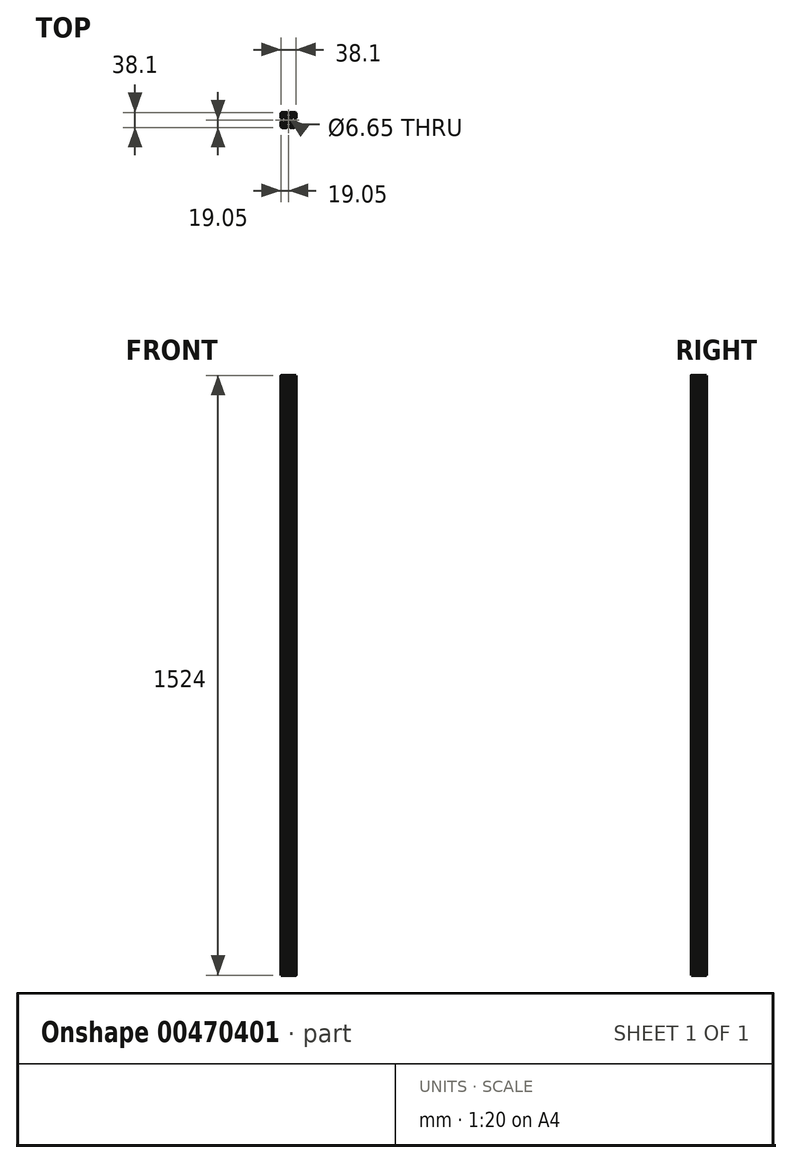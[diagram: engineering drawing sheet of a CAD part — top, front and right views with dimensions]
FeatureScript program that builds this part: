
annotation { "Feature Type Name" : "Feature", "Feature Type Description" : "" }
export const myFeature = defineFeature(function(context is Context, id is Id, definition is map)
    precondition{}
    {
        {
            var Q0;
            Q0=qCreatedBy(makeId("Top.planeOp"),FACE);
            var sketch = newSketch(context, id + "F0", { "sketchPlane" : qUnion([Q0])});
            skCircle(sketch, "E0", {"center": v(0, 0) * mm, "radius": 3.33 * mm});
            skArc(sketch, "E1", {"start": v(-10.29, 13.55) * mm, "mid": v(-10.22, 13.2) * mm, "end": v(-10.02, 12.91) * mm});
            skLineSegment(sketch, "E2", {"start": v(-10.29, 13.55) * mm, "end": v(-10.29, 14.08) * mm});
            skArc(sketch, "E3", {"start": v(-9.39, 14.99) * mm, "mid": v(-10.02, 14.72) * mm, "end": v(-10.29, 14.08) * mm});
            skLineSegment(sketch, "E4", {"start": v(-9.39, 14.99) * mm, "end": v(-5.62, 14.99) * mm});
            skArc(sketch, "E5", {"start": v(-5.62, 14.99) * mm, "mid": v(-4.52, 15.44) * mm, "end": v(-4.06, 16.54) * mm});
            skLineSegment(sketch, "E6", {"start": v(-4.06, 16.54) * mm, "end": v(-4.06, 17.5) * mm});
            skArc(sketch, "E7", {"start": v(-4.06, 17.5) * mm, "mid": v(-4.52, 18.6) * mm, "end": v(-5.62, 19.05) * mm});
            skLineSegment(sketch, "E8", {"start": v(-5.62, 19.05) * mm, "end": v(-7.97, 19.05) * mm});
            skArc(sketch, "E9", {"start": v(-9.5, 19.05) * mm, "mid": v(-8.74, 18.29) * mm, "end": v(-7.97, 19.05) * mm});
            skLineSegment(sketch, "E10", {"start": v(-9.5, 19.05) * mm, "end": v(-14.33, 19.05) * mm});
            skArc(sketch, "E11", {"start": v(-15.85, 19.05) * mm, "mid": v(-15.09, 18.23) * mm, "end": v(-14.33, 19.05) * mm});
            skArc(sketch, "E12", {"start": v(-15.85, 19.05) * mm, "mid": v(-18.12, 18.12) * mm, "end": v(-19.05, 15.85) * mm});
            skArc(sketch, "E13", {"start": v(-19.05, 14.33) * mm, "mid": v(-18.23, 15.09) * mm, "end": v(-19.05, 15.85) * mm});
            skLineSegment(sketch, "E14", {"start": v(-19.05, 14.33) * mm, "end": v(-19.05, 9.5) * mm});
            skArc(sketch, "E15", {"start": v(-19.05, 7.98) * mm, "mid": v(-18.23, 8.74) * mm, "end": v(-19.05, 9.5) * mm});
            skLineSegment(sketch, "E16", {"start": v(-19.05, 7.98) * mm, "end": v(-19.05, 5.62) * mm});
            skArc(sketch, "E17", {"start": v(-19.05, 5.62) * mm, "mid": v(-18.6, 4.52) * mm, "end": v(-17.5, 4.06) * mm});
            skLineSegment(sketch, "E18", {"start": v(-17.5, 4.06) * mm, "end": v(-16.54, 4.06) * mm});
            skArc(sketch, "E19", {"start": v(-16.54, 4.06) * mm, "mid": v(-15.44, 4.52) * mm, "end": v(-14.99, 5.62) * mm});
            skLineSegment(sketch, "E20", {"start": v(-14.99, 5.62) * mm, "end": v(-14.99, 9.39) * mm});
            skArc(sketch, "E21", {"start": v(-14.08, 10.29) * mm, "mid": v(-14.72, 10.02) * mm, "end": v(-14.99, 9.39) * mm});
            skLineSegment(sketch, "E22", {"start": v(-14.08, 10.29) * mm, "end": v(-13.52, 10.29) * mm});
            skArc(sketch, "E23", {"start": v(-12.88, 10.02) * mm, "mid": v(-13.17, 10.22) * mm, "end": v(-13.52, 10.29) * mm});
            skLineSegment(sketch, "E24", {"start": v(-12.88, 10.02) * mm, "end": v(-8.15, 5.3) * mm});
            skArc(sketch, "E25", {"start": v(-6.76, 1.93) * mm, "mid": v(-7.12, 3.75) * mm, "end": v(-8.15, 5.3) * mm});
            skLineSegment(sketch, "E26", {"start": v(-6.76, 1.93) * mm, "end": v(-6.76, -1.93) * mm});
            skArc(sketch, "E27", {"start": v(-8.15, -5.3) * mm, "mid": v(-7.12, -3.75) * mm, "end": v(-6.76, -1.93) * mm});
            skLineSegment(sketch, "E28", {"start": v(-8.15, -5.3) * mm, "end": v(-12.88, -10.02) * mm});
            skArc(sketch, "E29", {"start": v(-13.52, -10.29) * mm, "mid": v(-13.17, -10.22) * mm, "end": v(-12.88, -10.02) * mm});
            skLineSegment(sketch, "E30", {"start": v(-13.52, -10.29) * mm, "end": v(-14.08, -10.29) * mm});
            skArc(sketch, "E31", {"start": v(-14.99, -9.39) * mm, "mid": v(-14.72, -10.02) * mm, "end": v(-14.08, -10.29) * mm});
            skLineSegment(sketch, "E32", {"start": v(-14.99, -9.39) * mm, "end": v(-14.99, -5.62) * mm});
            skArc(sketch, "E33", {"start": v(-14.99, -5.62) * mm, "mid": v(-15.44, -4.52) * mm, "end": v(-16.54, -4.06) * mm});
            skLineSegment(sketch, "E34", {"start": v(-16.54, -4.06) * mm, "end": v(-17.5, -4.06) * mm});
            skArc(sketch, "E35", {"start": v(-17.5, -4.06) * mm, "mid": v(-18.6, -4.52) * mm, "end": v(-19.05, -5.62) * mm});
            skLineSegment(sketch, "E36", {"start": v(-19.05, -5.62) * mm, "end": v(-19.05, -7.98) * mm});
            skArc(sketch, "E37", {"start": v(-19.05, -9.5) * mm, "mid": v(-18.23, -8.74) * mm, "end": v(-19.05, -7.98) * mm});
            skLineSegment(sketch, "E38", {"start": v(-19.05, -9.5) * mm, "end": v(-19.05, -14.33) * mm});
            skArc(sketch, "E39", {"start": v(-19.05, -15.85) * mm, "mid": v(-18.23, -15.09) * mm, "end": v(-19.05, -14.33) * mm});
            skArc(sketch, "E40", {"start": v(-19.05, -15.85) * mm, "mid": v(-18.12, -18.12) * mm, "end": v(-15.85, -19.05) * mm});
            skArc(sketch, "E41", {"start": v(-14.33, -19.05) * mm, "mid": v(-15.09, -18.23) * mm, "end": v(-15.85, -19.05) * mm});
            skLineSegment(sketch, "E42", {"start": v(-14.33, -19.05) * mm, "end": v(-9.5, -19.05) * mm});
            skArc(sketch, "E43", {"start": v(-7.98, -19.05) * mm, "mid": v(-8.74, -18.23) * mm, "end": v(-9.5, -19.05) * mm});
            skLineSegment(sketch, "E44", {"start": v(-7.98, -19.05) * mm, "end": v(-5.62, -19.05) * mm});
            skArc(sketch, "E45", {"start": v(-5.62, -19.05) * mm, "mid": v(-4.52, -18.6) * mm, "end": v(-4.06, -17.5) * mm});
            skLineSegment(sketch, "E46", {"start": v(-4.06, -17.5) * mm, "end": v(-4.06, -16.54) * mm});
            skArc(sketch, "E47", {"start": v(-4.06, -16.54) * mm, "mid": v(-4.52, -15.44) * mm, "end": v(-5.62, -14.99) * mm});
            skLineSegment(sketch, "E48", {"start": v(-5.62, -14.99) * mm, "end": v(-9.39, -14.99) * mm});
            skArc(sketch, "E49", {"start": v(-10.29, -14.08) * mm, "mid": v(-10.02, -14.72) * mm, "end": v(-9.39, -14.99) * mm});
            skLineSegment(sketch, "E50", {"start": v(-10.29, -14.08) * mm, "end": v(-10.29, -13.55) * mm});
            skArc(sketch, "E51", {"start": v(-10.02, -12.91) * mm, "mid": v(-10.22, -13.2) * mm, "end": v(-10.29, -13.55) * mm});
            skLineSegment(sketch, "E52", {"start": v(-10.02, -12.91) * mm, "end": v(-5.25, -8.14) * mm});
            skArc(sketch, "E53", {"start": v(-1.9, -6.76) * mm, "mid": v(-3.72, -7.12) * mm, "end": v(-5.25, -8.14) * mm});
            skLineSegment(sketch, "E54", {"start": v(-1.9, -6.76) * mm, "end": v(1.9, -6.76) * mm});
            skArc(sketch, "E55", {"start": v(5.25, -8.14) * mm, "mid": v(3.72, -7.12) * mm, "end": v(1.9, -6.76) * mm});
            skLineSegment(sketch, "E56", {"start": v(5.25, -8.14) * mm, "end": v(10.02, -12.91) * mm});
            skArc(sketch, "E57", {"start": v(10.29, -13.55) * mm, "mid": v(10.22, -13.2) * mm, "end": v(10.02, -12.91) * mm});
            skLineSegment(sketch, "E58", {"start": v(10.29, -13.55) * mm, "end": v(10.29, -14.08) * mm});
            skArc(sketch, "E59", {"start": v(9.39, -14.99) * mm, "mid": v(10.02, -14.72) * mm, "end": v(10.29, -14.08) * mm});
            skLineSegment(sketch, "E60", {"start": v(9.39, -14.99) * mm, "end": v(5.62, -14.99) * mm});
            skArc(sketch, "E61", {"start": v(5.62, -14.99) * mm, "mid": v(4.52, -15.44) * mm, "end": v(4.06, -16.54) * mm});
            skLineSegment(sketch, "E62", {"start": v(4.06, -16.54) * mm, "end": v(4.06, -17.5) * mm});
            skArc(sketch, "E63", {"start": v(4.06, -17.5) * mm, "mid": v(4.52, -18.6) * mm, "end": v(5.62, -19.05) * mm});
            skLineSegment(sketch, "E64", {"start": v(5.62, -19.05) * mm, "end": v(7.98, -19.05) * mm});
            skArc(sketch, "E65", {"start": v(9.5, -19.05) * mm, "mid": v(8.74, -18.23) * mm, "end": v(7.98, -19.05) * mm});
            skLineSegment(sketch, "E66", {"start": v(9.5, -19.05) * mm, "end": v(14.33, -19.05) * mm});
            skArc(sketch, "E67", {"start": v(15.85, -19.05) * mm, "mid": v(15.09, -18.23) * mm, "end": v(14.33, -19.05) * mm});
            skArc(sketch, "E68", {"start": v(15.85, -19.05) * mm, "mid": v(18.12, -18.12) * mm, "end": v(19.05, -15.85) * mm});
            skArc(sketch, "E69", {"start": v(19.05, -14.33) * mm, "mid": v(18.23, -15.09) * mm, "end": v(19.05, -15.85) * mm});
            skLineSegment(sketch, "E70", {"start": v(19.05, -14.33) * mm, "end": v(19.05, -9.5) * mm});
            skArc(sketch, "E71", {"start": v(19.05, -7.98) * mm, "mid": v(18.23, -8.74) * mm, "end": v(19.05, -9.5) * mm});
            skLineSegment(sketch, "E72", {"start": v(19.05, -7.98) * mm, "end": v(19.05, -5.62) * mm});
            skArc(sketch, "E73", {"start": v(19.05, -5.62) * mm, "mid": v(18.6, -4.52) * mm, "end": v(17.5, -4.06) * mm});
            skLineSegment(sketch, "E74", {"start": v(17.5, -4.06) * mm, "end": v(16.54, -4.06) * mm});
            skArc(sketch, "E75", {"start": v(16.54, -4.06) * mm, "mid": v(15.44, -4.52) * mm, "end": v(14.99, -5.62) * mm});
            skLineSegment(sketch, "E76", {"start": v(14.99, -5.62) * mm, "end": v(14.99, -9.39) * mm});
            skArc(sketch, "E77", {"start": v(14.08, -10.29) * mm, "mid": v(14.72, -10.02) * mm, "end": v(14.99, -9.39) * mm});
            skLineSegment(sketch, "E78", {"start": v(14.08, -10.29) * mm, "end": v(13.52, -10.29) * mm});
            skArc(sketch, "E79", {"start": v(12.88, -10.02) * mm, "mid": v(13.17, -10.22) * mm, "end": v(13.52, -10.29) * mm});
            skLineSegment(sketch, "E80", {"start": v(12.88, -10.02) * mm, "end": v(8.15, -5.3) * mm});
            skArc(sketch, "E81", {"start": v(6.76, -1.93) * mm, "mid": v(7.12, -3.75) * mm, "end": v(8.15, -5.3) * mm});
            skLineSegment(sketch, "E82", {"start": v(6.76, -1.93) * mm, "end": v(6.76, 1.93) * mm});
            skArc(sketch, "E83", {"start": v(8.15, 5.3) * mm, "mid": v(7.12, 3.75) * mm, "end": v(6.76, 1.93) * mm});
            skLineSegment(sketch, "E84", {"start": v(8.15, 5.3) * mm, "end": v(12.88, 10.02) * mm});
            skArc(sketch, "E85", {"start": v(13.52, 10.29) * mm, "mid": v(13.17, 10.22) * mm, "end": v(12.88, 10.02) * mm});
            skLineSegment(sketch, "E86", {"start": v(13.52, 10.29) * mm, "end": v(14.08, 10.29) * mm});
            skArc(sketch, "E87", {"start": v(14.99, 9.39) * mm, "mid": v(14.72, 10.02) * mm, "end": v(14.08, 10.29) * mm});
            skLineSegment(sketch, "E88", {"start": v(14.99, 9.39) * mm, "end": v(14.99, 5.62) * mm});
            skArc(sketch, "E89", {"start": v(14.99, 5.62) * mm, "mid": v(15.44, 4.52) * mm, "end": v(16.54, 4.06) * mm});
            skLineSegment(sketch, "E90", {"start": v(16.54, 4.06) * mm, "end": v(17.5, 4.06) * mm});
            skArc(sketch, "E91", {"start": v(17.5, 4.06) * mm, "mid": v(18.6, 4.52) * mm, "end": v(19.05, 5.62) * mm});
            skLineSegment(sketch, "E92", {"start": v(19.05, 5.62) * mm, "end": v(19.05, 7.98) * mm});
            skArc(sketch, "E93", {"start": v(19.05, 9.5) * mm, "mid": v(18.23, 8.74) * mm, "end": v(19.05, 7.98) * mm});
            skLineSegment(sketch, "E94", {"start": v(19.05, 9.5) * mm, "end": v(19.05, 14.33) * mm});
            skArc(sketch, "E95", {"start": v(19.05, 15.85) * mm, "mid": v(18.23, 15.09) * mm, "end": v(19.05, 14.33) * mm});
            skArc(sketch, "E96", {"start": v(19.05, 15.85) * mm, "mid": v(18.12, 18.12) * mm, "end": v(15.85, 19.05) * mm});
            skArc(sketch, "E97", {"start": v(14.33, 19.05) * mm, "mid": v(15.09, 18.23) * mm, "end": v(15.85, 19.05) * mm});
            skLineSegment(sketch, "E98", {"start": v(14.33, 19.05) * mm, "end": v(9.5, 19.05) * mm});
            skArc(sketch, "E99", {"start": v(7.97, 19.05) * mm, "mid": v(8.74, 18.29) * mm, "end": v(9.5, 19.05) * mm});
            skLineSegment(sketch, "E100", {"start": v(7.97, 19.05) * mm, "end": v(5.62, 19.05) * mm});
            skArc(sketch, "E101", {"start": v(5.62, 19.05) * mm, "mid": v(4.52, 18.6) * mm, "end": v(4.06, 17.5) * mm});
            skLineSegment(sketch, "E102", {"start": v(4.06, 17.5) * mm, "end": v(4.06, 16.54) * mm});
            skArc(sketch, "E103", {"start": v(4.06, 16.54) * mm, "mid": v(4.52, 15.44) * mm, "end": v(5.62, 14.99) * mm});
            skLineSegment(sketch, "E104", {"start": v(5.62, 14.99) * mm, "end": v(9.39, 14.99) * mm});
            skArc(sketch, "E105", {"start": v(10.29, 14.08) * mm, "mid": v(10.02, 14.72) * mm, "end": v(9.39, 14.99) * mm});
            skLineSegment(sketch, "E106", {"start": v(10.29, 14.08) * mm, "end": v(10.29, 13.55) * mm});
            skArc(sketch, "E107", {"start": v(10.02, 12.91) * mm, "mid": v(10.22, 13.2) * mm, "end": v(10.29, 13.55) * mm});
            skLineSegment(sketch, "E108", {"start": v(10.02, 12.91) * mm, "end": v(5.25, 8.14) * mm});
            skArc(sketch, "E109", {"start": v(1.9, 6.76) * mm, "mid": v(3.72, 7.12) * mm, "end": v(5.25, 8.14) * mm});
            skLineSegment(sketch, "E110", {"start": v(1.9, 6.76) * mm, "end": v(-1.9, 6.76) * mm});
            skArc(sketch, "E111", {"start": v(-5.25, 8.14) * mm, "mid": v(-3.72, 7.12) * mm, "end": v(-1.9, 6.76) * mm});
            skLineSegment(sketch, "E112", {"start": v(-5.25, 8.14) * mm, "end": v(-10.02, 12.91) * mm});
            skSolve(sketch);
        }
        {
            var Q0;
            Q0 = qSketchRegion(id + "F0", true);
            extrude(context, id + "F1", {"entities" : qUnion([Q0]), "depth" : 1524 * mm});
        }
    });
